# Revit family: IS_UltraflatII_T4467_BIM_NL
name_source: partatom
category: Plumbing Fixtures
revit_build: Autodesk Revit 2017 (Build: 20160225_1515(x64)
units: mm (PartAtom-declared; Revit-internal decimal feet)

## family parameters
Always vertical = No
Cut with Voids When Loaded = No
OmniClass Number = 23.45.05.14.17
OmniClass Title = Showers
Part Type = Normal
Room Calculation Point = No
Round Connector Dimension = Use Diameter
Shared = No
Work Plane-Based = No

## types (2) — shared parameters
Accesoires = https://www.idealstandardnederland.nl
Afmetingen = 900 x 900 x 25 mm
Artikelomschrijving = Ultra-Flat 2 Duschwanne 900 x 900mm, Quadrat. Erhältlich in 2 fertigen Weiß und Satin Weiß.
Artikelreferentie = ULTRAFLAT 2 SHT 90X90 SQ  WHITE
Auteur = Ideal Standard
BIMobject category code = sanitary-shower-trays
BIMobject main category = Sanitary
BIMobject main category code = sanitary
Beschrijvinggarantie = fabrieksgarantie
Brand url = https://www.idealstandardnederland.nl
Breedte = 900.000031
Date of publishing = 15/12/2020
Douchebak = No
DuurEenheid = Jaren
Duurzaamheid = 5
Edition number = 1
Eigenschappen = Duschwanne 900 x 900mm, Quadrat. Erhältlich in 2 fertigen Weiß und Satin Weiß.
Garantieonderdelen = 5
Garantieunits = Jaren
Heefthandvaten = No
Hoogte = 24.906137
IFC Classification = Sanitary Terminal
Installatieinstructies = https://www.idealstandardnederland.nl
Installation instructions = https://www.idealstandardnederland.nl
Lengte = 900 mm
Manufacturer = Ideal Standard Netherlands
Manufacturer name = Ideal Standard
Masterformat 2014 Code = 10 21 16
Masterformat 2014 Description = Shower and Dressing compartements
Materiaal = hars
Material main = Resin
Merk = Ideal Standard GmbH
Montageinstuctie = https://www.idealstandardnederland.nl
NBS Reference Code = 45-35-70/336
NBS Reference Description = Shower trays
NominalHeight = 25 mm
NominalLength = 900 mm
NominalWidth = 900 mm
OmniClass Code = 23-15 11 15 13
OmniClass Description = Shower and Dressing Compartments
OppervlakteEenheid = millimeter
Product Guid = b661bae1-af0a-4bcf-a5c4-599a0926a536
Product SKU = T4467
Product data url = https://bimobject.com
Product family = ULTRA FLAT
Product group = Shower Tray
Product name = ULTRAFLAT 2 SHT 90X90 SQ
Product url = https://www.idealstandardnederland.nl
Productinformatie = https://www.idealstandardnederland.nl
QR code = https://www.idealstandardnederland.nl
Referentie = ULTRAFLAT 2 SHT 90X90 SQ  WHITE
Revisie = 1
Size = 900 x 900 x 25 mm
Technical description = https://www.idealstandardnederland.nl
Telefoonnummer = (077) 355 08 08
Typeconnectie = loodgieter
UNSPSC Code = 301815
URL = https://www.idealstandard.nl
Uniclass 1.4 Code = L72143
Uniclass 1.4 Description = Shower trays
Uniclass 2.0 Code = PR-35-06-84
Uniclass 2.0 Description = Shower Trays
Uniclass 2015 Code = Pr_40_20_06_84
Uniclass 2015 Name = Shower trays
Uniclass2015Referentie = Shower trays
Urlproducent = https://www.idealstandard.nl
ValutaEenheid = €
Versie = 1
Volumeunits = Liter
Vorm = rechthoekig
Wisselstukken = https://www.idealstandardnederland.nl
zero-valued in all types: BrutoGewicht, Diepte, GrootteAfvoergat, Nettogewicht, Overloop, Vervangingskosten

## per-type parameters (varying)
| type | Artikelnummer | Description | GTIN code | Model |
| T446701 - ULTRAFLAT 2 SHT 90X90 SQUARE - Glossy White | T446701 | Ultraflat2 Shower Tray 900 x 900mm, Square with Glossy White Finish. | 8014140481805 | T446701 |
| T4467V1 - ULTRAFLAT 2 SHT 90X90 SQUARE - Silk White | T4467V1 | Ultraflat2 Shower Tray 900 x 900mm, Square with Silk White Finish. | 8014140481812 | T4467V1 |

## geometry (parser evidence)
native form markers: Sweep x3
no freeform markers — native parametric forms only
